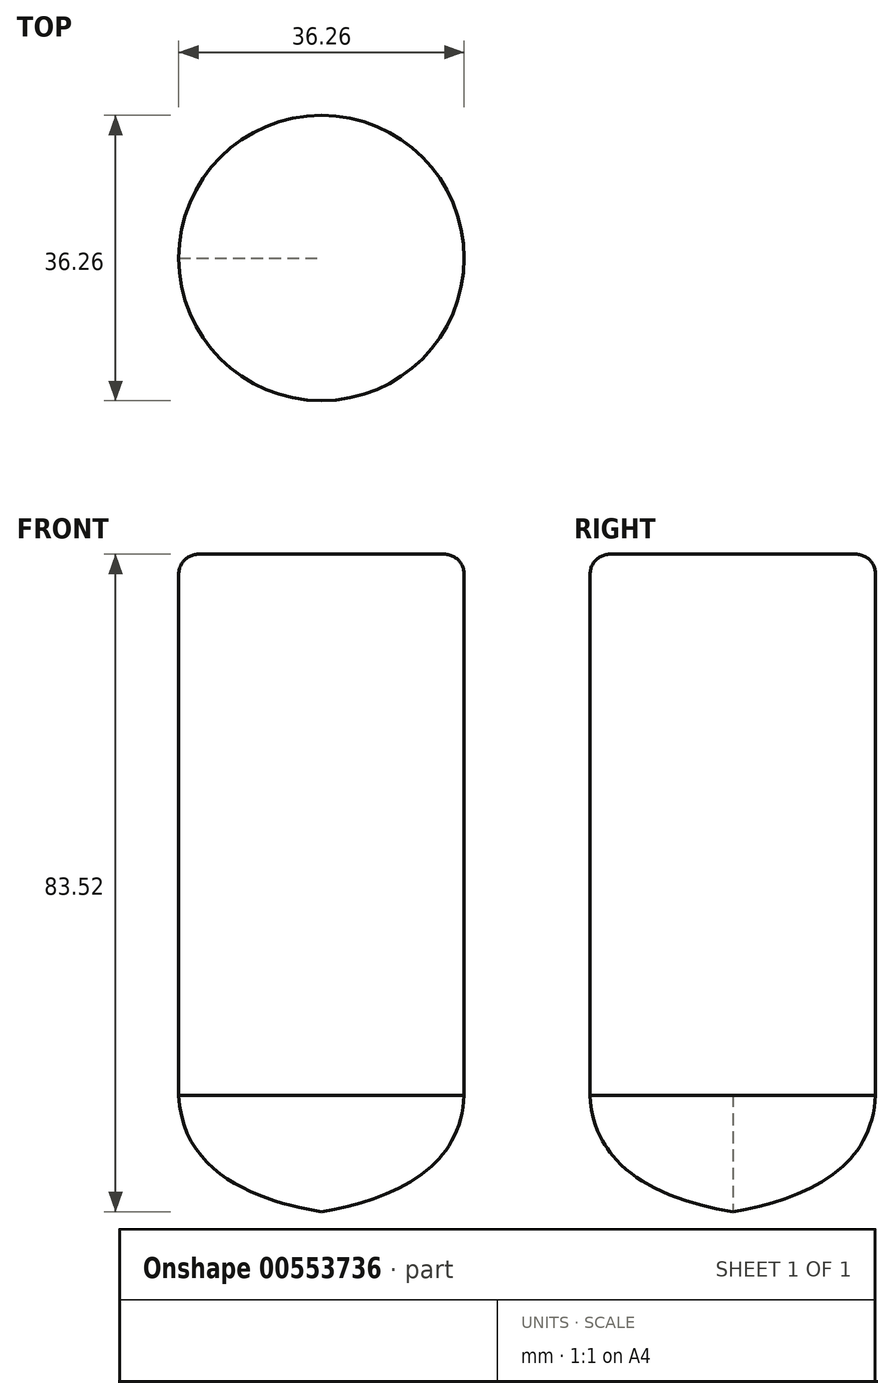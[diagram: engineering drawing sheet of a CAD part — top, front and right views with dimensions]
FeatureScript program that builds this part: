
annotation { "Feature Type Name" : "Feature", "Feature Type Description" : "" }
export const myFeature = defineFeature(function(context is Context, id is Id, definition is map)
    precondition{}
    {
        {
            var Q0;
            Q0=qCreatedBy(makeId("Front.planeOp"),FACE);
            var sketch = newSketch(context, id + "F0", { "sketchPlane" : qUnion([Q0])});
            skLineSegment(sketch, "E0", {"start": v(-18.13, 29.46) * mm, "end": v(-18.13, -36.73) * mm});
            skFitSpline(sketch, "E1", {"points": [v(-18.13, -36.73) * mm, v(0, -51.52) * mm], "startDerivative": vector(1.32, -31.39) * mm, "endDerivative": vector(20.7, -3.35) * mm});
            skLineSegment(sketch, "E2", {"start": v(-15.6, 32) * mm, "end": v(0, 32) * mm});
            skPoint(sketch, "E3.visualSharp", {"position": v(-18.13, 32) * mm});
            skArc(sketch, "E3.filletArc", {"start": v(-15.6, 32) * mm, "mid": v(-17.39, 31.26) * mm, "end": v(-18.13, 29.46) * mm});
            skLineSegment(sketch, "E4", {"start": v(0, 32) * mm, "end": v(0, -51.52) * mm});
            skSolve(sketch);
        }
        {
            var Q0;
            Q0=makeQuery(id+"F0.imprint","IMPRINT",FACE,{"disambiguationData":[TD([[makeQuery(id+"F0.imprint","IMPRINT",EDGE,{"derivedFrom":sQuery(id+"F0.wireOp",EDGE,"E0")}),1.0]])]});
            var Q1;
            Q1=sQuery(id+"F0.wireOp",EDGE,"E4");
            revolve(context, id + "F1", {"entities" : qUnion([Q0]), "axis" : qUnion([Q1]), "revolveType" : RevolveType.FULL});
        }
    });
